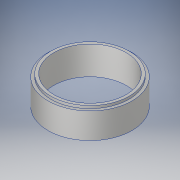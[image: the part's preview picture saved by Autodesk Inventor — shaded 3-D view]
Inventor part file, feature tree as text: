
AUTODESK INVENTOR PART (.ipt)
format: ipt  version: 2017 (Build 210142000, 142)  size: 150,016 bytes
history: native  units: in
note: dims shown in document units (in); Inventor stores cm internally (conversion verified against a paired STEP export)
features: revolve x1, sketch x1
ambient origin geometry x8: Origin, YZ Plane, XZ Plane, XY Plane, X Axis, Y Axis, Z Axis, Center Point
bodies: Solid1 (feature_tree)
feature tree (2):
  revolve  "Revolution1"  [1 undecoded]
  sketch  "Sketch1"  dims[d0=1.13in d1=3.7in d2=0.125in d3=0.1718in d5=1.0in d6=1.0in d7=90.0deg d8=0.5in d9=15.0deg d12=1.25in d13=0.25in d16=0.5in d17=0.5in d18=0.5in d19=2.5in d20=0.5in d22=0.375in d23=0.25in d25=0.234in d26=15.0deg d27=0.125in d28=0.25in d29=1.0in d30=4.25in d31=0.25in d32=1.0in d33=90.0deg]
note: 1 required parameter value undecoded (feature->parameter linkage not recoverable at this tier; creation-order binding heuristic only, values carry confidence <= 0.55)
